# Revit family: Mesa Gavarres
name_source: partatom
category: Furniture
units: mm (PartAtom-declared; Revit-internal decimal feet)

## family parameters
Always vertical = Yes
Cut with Voids When Loaded = No
OmniClass Number = 23.40.20.00
OmniClass Title = General Furniture and Specialties
Room Calculation Point = No
Shared = No
Work Plane-Based = No

## types (1)
- Mesa Gavarres-VM311-2040mm
    A = 2.04 m
    B = 0.67 m
    C = 0.4 m
    Default Elevation = 0 m
    Description = Mesa fabricada en madera de pino tratada en autoclave a vacío-presión clase 4 contra la carcoma, termitas e insectos. Tornillería de acero
inoxidable. Pies en plancha de acero corten de 8 mm
    Fabricante = BENITO URBAN SL
    Ficha_Tecnica = https://www.benito.com
    H = 0.81 m
    H1 = 0.44 m
    Material = Madera de pino
    Referencia = VM311
    Type Comments = Anclaje recomendado: Mediante pernos de expansión M10, según superficie y instalación.
    URL_Producto = https://www.benito.com

## geometry (parser evidence)
native form markers: Blend x2, Sweep x3
no freeform markers — native parametric forms only
